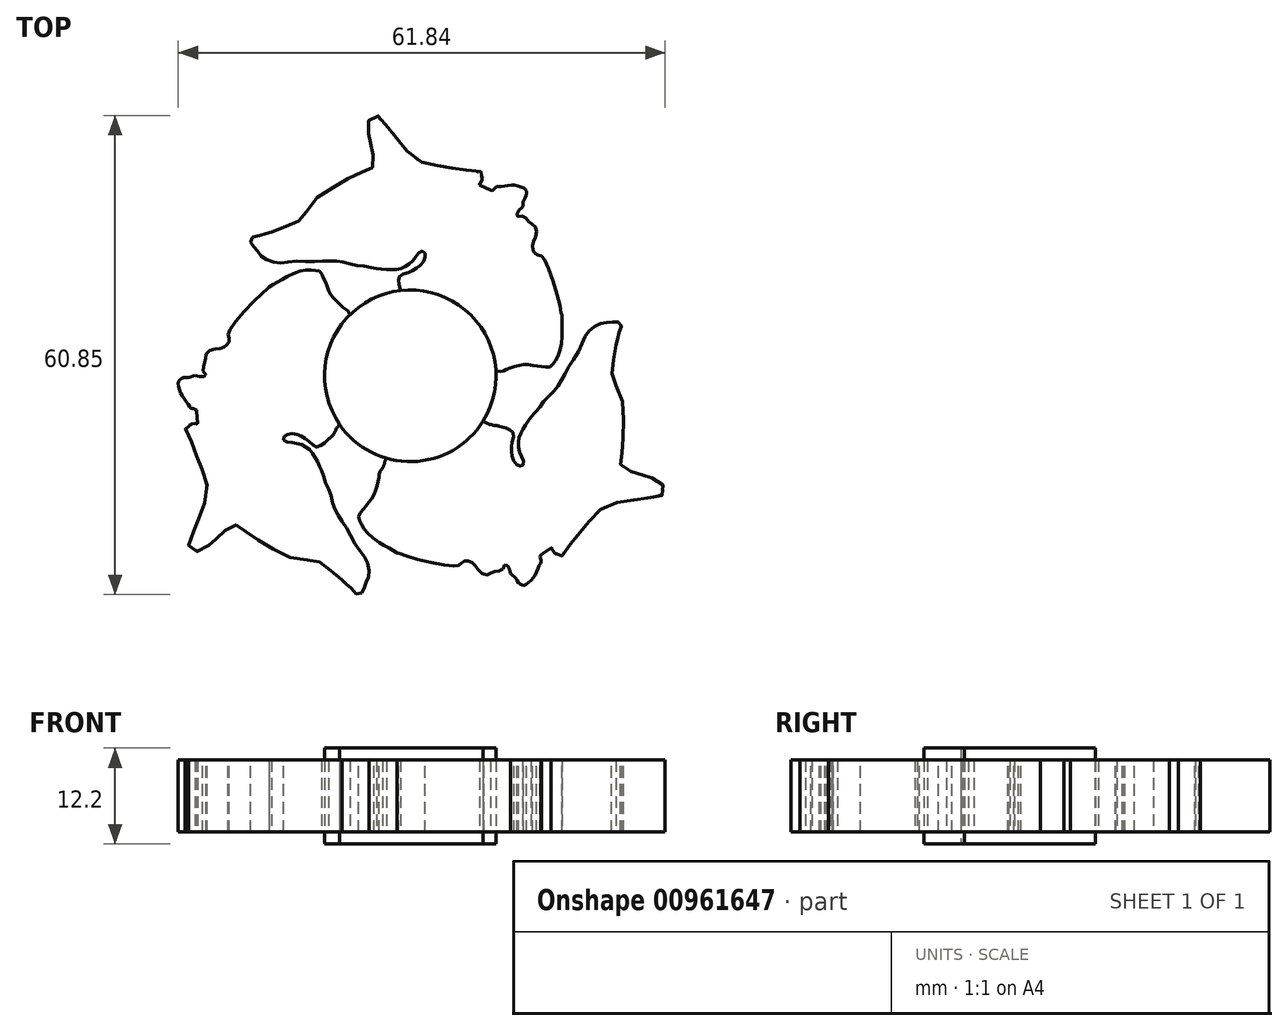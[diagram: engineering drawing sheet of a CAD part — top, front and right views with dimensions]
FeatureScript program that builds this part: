
annotation { "Feature Type Name" : "Feature", "Feature Type Description" : "" }
export const myFeature = defineFeature(function(context is Context, id is Id, definition is map)
    precondition{}
    {
        {
            var Q0;
            Q0=qCreatedBy(makeId("Top.planeOp"),FACE);
            var sketch = newSketch(context, id + "F0", { "sketchPlane" : qUnion([Q0])});
            skCircle(sketch, "E0", {"center": v(-5.45, -7.26) * mm, "radius": 10.9 * mm});
            skFitSpline(sketch, "E1", {"points": [v(-6.67, 3.57) * mm, v(-6.92, 4.58) * mm, v(-6.88, 5.09) * mm, v(-6.68, 5.56) * mm, v(-5.87, 5.8) * mm, v(-5.19, 6.1) * mm, v(-4.58, 6.45) * mm, v(-4.1, 6.82) * mm, v(-3.63, 7.5) * mm, v(-3.56, 8.14) * mm, v(-3.7, 8.48) * mm, v(-4.07, 8.55) * mm, v(-4.54, 8.14) * mm, v(-4.98, 7.53) * mm, v(-5.5, 6.99) * mm, v(-6.17, 6.58) * mm, v(-6.78, 6.3) * mm, v(-7.6, 6.24) * mm, v(-8.14, 6.2) * mm, v(-9.06, 6.3) * mm, v(-9.7, 6.34) * mm], "startDerivative": vector(-5.28, 17.85) * mm, "endDerivative": vector(-12.23, 0.24) * mm});
            skFitSpline(sketch, "E2", {"points": [v(-9.7, 6.34) * mm, v(-10.39, 6.45) * mm, v(-11.53, 6.73) * mm, v(-12.4, 6.77) * mm, v(-13.56, 7.07) * mm, v(-14.58, 7.31) * mm, v(-15.53, 7.34) * mm, v(-16.65, 7.31) * mm, v(-18, 7.24) * mm, v(-19.8, 7.31) * mm, v(-21.34, 7.16) * mm, v(-22.42, 7.1) * mm, v(-23.45, 7.39) * mm, v(-24.33, 7.89) * mm, v(-24.83, 8.5) * mm, v(-25.3, 9.11) * mm, v(-25.68, 9.65) * mm, v(-25.62, 10.26) * mm, v(-24.73, 10.54) * mm, v(-23.75, 10.84) * mm, v(-23.04, 11.01) * mm], "startDerivative": vector(-15.19, 1.76) * mm, "endDerivative": vector(16.2, 3.23) * mm});
            skFitSpline(sketch, "E3", {"points": [v(-23.04, 11.01) * mm, v(-21.41, 11.66) * mm, v(-19.99, 12.28) * mm, v(-19.13, 12.68) * mm, v(-18.16, 14.45) * mm, v(-16.28, 16.05) * mm, v(-14, 17.42) * mm, v(-12.28, 18.28) * mm, v(-10.86, 18.9) * mm, v(-10.23, 19.25) * mm, v(-10.11, 20.44) * mm, v(-10.4, 21.76) * mm, v(-10.57, 22.61) * mm, v(-10.74, 23.24) * mm, v(-10.74, 24.55) * mm, v(-10.57, 25.52) * mm, v(-9.54, 25.75) * mm, v(-8.4, 24.44) * mm, v(-7.55, 23.35) * mm, v(-6.35, 21.87) * mm, v(-4.46, 20.1) * mm, v(-2.35, 19.47) * mm, v(-0.81, 19.25) * mm, v(1, 18.96) * mm, v(2.5, 18.79) * mm, v(3.8, 18.5) * mm, v(3.8, 17.85) * mm, v(3.53, 17.52) * mm, v(3.39, 17.18) * mm, v(3.36, 16.97) * mm], "startDerivative": vector(41.16, 15.32) * mm, "endDerivative": vector(-0.65, -14.42) * mm});
            skLineSegment(sketch, "E4", {"start": v(3.36, 16.97) * mm, "end": v(4.72, 16.33) * mm});
            skFitSpline(sketch, "E5", {"points": [v(4.72, 16.33) * mm, v(4.86, 16.3) * mm, v(5.01, 16.33) * mm, v(5.18, 16.45) * mm, v(5.35, 16.64) * mm, v(5.52, 16.78) * mm, v(5.72, 16.8) * mm, v(6.45, 16.84) * mm, v(7.5, 16.96) * mm, v(8.3, 16.84) * mm, v(9.06, 16.54) * mm, v(9.26, 16.33) * mm, v(9.33, 15.94) * mm, v(9.24, 15.52) * mm, v(9, 15.08) * mm, v(8.87, 14.66) * mm, v(8.79, 14.2) * mm, v(8.78, 14.18) * mm], "startDerivative": vector(3.87, -1.54) * mm, "endDerivative": vector(-0.93, -0.4) * mm});
            skFitSpline(sketch, "E6", {"points": [v(8.79, 14.2) * mm, v(8.24, 13.6) * mm, v(8.12, 13.03) * mm, v(8.79, 13.05) * mm, v(9.4, 12.55) * mm, v(9.92, 12.07) * mm, v(10.52, 11.51) * mm, v(10.43, 10.27) * mm, v(10.09, 9.45) * mm, v(10.16, 8.73) * mm, v(10.38, 8.3) * mm, v(11, 8.03) * mm, v(11.48, 7.7) * mm, v(13.47, 2.07) * mm, v(13.8, 0.43) * mm, v(13.82, 0.43) * mm], "startDerivative": vector(-9.43, -8) * mm, "endDerivative": vector(2.22, 0.73) * mm});
            skFitSpline(sketch, "E7", {"points": [v(13.82, 0.43) * mm, v(13.82, -0.64) * mm, v(13.82, -2.3) * mm, v(13.42, -4.52) * mm, v(12.79, -5.58) * mm, v(12.22, -6.15) * mm, v(11.25, -6.06) * mm, v(10.48, -6) * mm, v(9.36, -5.83) * mm, v(8.34, -5.98) * mm, v(7.3, -6.23) * mm, v(6.54, -6.52) * mm, v(6.25, -6.7) * mm, v(5.43, -6.63) * mm], "startDerivative": vector(-0.14, -13.17) * mm, "endDerivative": vector(-14.05, 2.29) * mm});
            skFitSpline(sketch, "E8", {"points": [v(5.97, -13.68) * mm, v(6.97, -13.98) * mm, v(7.39, -14.27) * mm, v(7.7, -14.68) * mm, v(7.49, -15.5) * mm, v(7.4, -16.25) * mm, v(7.39, -16.95) * mm, v(7.47, -17.54) * mm, v(7.82, -18.3) * mm, v(8.34, -18.68) * mm, v(8.7, -18.74) * mm, v(8.95, -18.45) * mm, v(8.84, -17.83) * mm, v(8.53, -17.14) * mm, v(8.32, -16.43) * mm, v(8.31, -15.64) * mm, v(8.4, -14.97) * mm, v(8.74, -14.24) * mm, v(8.99, -13.75) * mm, v(9.54, -13.01) * mm, v(9.9, -12.48) * mm], "startDerivative": vector(18.06, -4.49) * mm, "endDerivative": vector(6.4, 10.43) * mm});
            skFitSpline(sketch, "E9", {"points": [v(9.9, -12.48) * mm, v(10.34, -11.94) * mm, v(11.15, -11.1) * mm, v(11.64, -10.36) * mm, v(12.48, -9.52) * mm, v(13.2, -8.76) * mm, v(13.71, -7.96) * mm, v(14.25, -6.97) * mm, v(14.88, -5.77) * mm, v(15.85, -4.25) * mm, v(16.5, -2.86) * mm, v(17, -1.9) * mm, v(17.76, -1.15) * mm, v(18.64, -0.65) * mm, v(19.42, -0.52) * mm, v(20.2, -0.42) * mm, v(20.85, -0.37) * mm, v(21.34, -0.74) * mm, v(21.13, -1.64) * mm, v(20.9, -2.64) * mm, v(20.68, -3.34) * mm], "startDerivative": vector(9.2, 12.2) * mm, "endDerivative": vector(-5.43, -15.6) * mm});
            skFitSpline(sketch, "E10", {"points": [v(20.68, -3.34) * mm, v(20.41, -5.07) * mm, v(20.23, -6.62) * mm, v(20.14, -7.56) * mm, v(21.17, -9.29) * mm, v(21.6, -11.72) * mm, v(21.62, -14.38) * mm, v(21.5, -16.3) * mm, v(21.31, -17.84) * mm, v(21.29, -18.56) * mm, v(22.26, -19.26) * mm, v(23.54, -19.68) * mm, v(24.37, -19.97) * mm, v(25, -20.14) * mm, v(26.12, -20.8) * mm, v(26.87, -21.44) * mm, v(26.55, -22.44) * mm, v(24.84, -22.76) * mm, v(23.47, -22.95) * mm, v(21.59, -23.23) * mm, v(19.1, -23.96) * mm, v(17.5, -25.46) * mm, v(16.52, -26.68) * mm, v(15.35, -28.09) * mm, v(14.45, -29.3) * mm, v(13.54, -30.28) * mm, v(12.99, -29.94) * mm, v(12.83, -29.55) * mm, v(12.61, -29.25) * mm, v(12.44, -29.12) * mm], "startDerivative": vector(-7.64, -43.24) * mm, "endDerivative": vector(-12.1, 7.87) * mm});
            skLineSegment(sketch, "E11", {"start": v(12.44, -29.12) * mm, "end": v(11.2, -29.97) * mm});
            skFitSpline(sketch, "E12", {"points": [v(11.2, -29.97) * mm, v(11.1, -30.07) * mm, v(11.06, -30.22) * mm, v(11.08, -30.43) * mm, v(11.15, -30.67) * mm, v(11.18, -30.88) * mm, v(11.1, -31.06) * mm, v(10.76, -31.72) * mm, v(10.34, -32.68) * mm, v(9.82, -33.32) * mm, v(9.19, -33.82) * mm, v(8.9, -33.88) * mm, v(8.54, -33.75) * mm, v(8.22, -33.46) * mm, v(7.96, -33.02) * mm, v(7.66, -32.7) * mm, v(7.3, -32.4) * mm, v(7.3, -32.38) * mm], "startDerivative": vector(-3.29, -2.55) * mm, "endDerivative": vector(0.13, 1) * mm});
            skFitSpline(sketch, "E13", {"points": [v(7.3, -32.4) * mm, v(7.07, -31.62) * mm, v(6.63, -31.23) * mm, v(6.31, -31.81) * mm, v(5.57, -32.08) * mm, v(4.9, -32.3) * mm, v(4.11, -32.53) * mm, v(3.08, -31.82) * mm, v(2.55, -31.11) * mm, v(1.9, -30.81) * mm, v(1.41, -30.78) * mm, v(0.87, -31.18) * mm, v(0.34, -31.43) * mm, v(-5.53, -30.3) * mm, v(-7.1, -29.74) * mm, v(-7.11, -29.76) * mm], "startDerivative": vector(-2.13, 12.18) * mm, "endDerivative": vector(-0.5, -2.29) * mm});
            skFitSpline(sketch, "E14", {"points": [v(-7.11, -29.76) * mm, v(-8.04, -29.22) * mm, v(-9.47, -28.38) * mm, v(-11.18, -26.9) * mm, v(-11.77, -25.83) * mm, v(-11.98, -25.05) * mm, v(-11.4, -24.25) * mm, v(-10.97, -23.62) * mm, v(-10.26, -22.74) * mm, v(-9.86, -21.79) * mm, v(-9.56, -20.77) * mm, v(-9.42, -19.96) * mm, v(-9.42, -19.63) * mm, v(-8.96, -18.95) * mm], "startDerivative": vector(-11.29, 6.8) * mm, "endDerivative": vector(9.09, 10.95) * mm});
            skLineSegment(sketch, "E15.0", {"start": v(11.2, -29.97) * mm, "end": v(8.9, -33.88) * mm, "construction": true});
            skLineSegment(sketch, "E16.0", {"start": v(-9.47, -28.38) * mm, "end": v(-7.11, -29.76) * mm, "construction": true});
            skLineSegment(sketch, "E17.0", {"start": v(6.31, -31.81) * mm, "end": v(7.3, -32.4) * mm, "construction": true});
            skFitSpline(sketch, "E18", {"points": [v(5.97, -13.68) * mm, v(5.64, -13.6) * mm, v(5.24, -13.56) * mm, v(4.98, -13.51) * mm, v(4.82, -13.46) * mm, v(4.56, -13.4) * mm, v(4.29, -13.3) * mm, v(3.81, -13) * mm, v(3.8, -13.01) * mm], "startDerivative": vector(-2.22, 0.55) * mm, "endDerivative": vector(-0.03, -0.43) * mm});
            skFitSpline(sketch, "E19", {"points": [v(-8.96, -18.95) * mm, v(-8.82, -18.65) * mm, v(-8.72, -18.4) * mm, v(-8.69, -18.2) * mm, v(-8.61, -17.97) * mm, v(-8.54, -17.83) * mm, v(-8.48, -17.73) * mm], "startDerivative": vector(0.65, 1.48) * mm, "endDerivative": vector(0.53, 0.83) * mm});
            skFitSpline(sketch, "E20", {"points": [v(-15.83, -15.28) * mm, v(-16.58, -16) * mm, v(-17.04, -16.22) * mm, v(-17.55, -16.28) * mm, v(-18.16, -15.7) * mm, v(-18.77, -15.26) * mm, v(-19.37, -14.9) * mm, v(-19.93, -14.68) * mm, v(-20.75, -14.6) * mm, v(-21.34, -14.87) * mm, v(-21.57, -15.16) * mm, v(-21.44, -15.51) * mm, v(-20.85, -15.72) * mm, v(-20.1, -15.8) * mm, v(-19.38, -15.97) * mm, v(-18.69, -16.35) * mm, v(-18.14, -16.74) * mm, v(-17.68, -17.42) * mm, v(-17.38, -17.87) * mm, v(-17, -18.71) * mm, v(-16.72, -19.29) * mm], "startDerivative": vector(-12.82, -13.5) * mm, "endDerivative": vector(5.9, -10.71) * mm});
            skFitSpline(sketch, "E21", {"points": [v(-16.72, -19.29) * mm, v(-16.47, -19.94) * mm, v(-16.13, -21.06) * mm, v(-15.73, -21.85) * mm, v(-15.42, -23) * mm, v(-15.11, -24) * mm, v(-14.67, -24.84) * mm, v(-14.08, -25.8) * mm, v(-13.34, -26.93) * mm, v(-12.5, -28.52) * mm, v(-11.6, -29.77) * mm, v(-11.01, -30.68) * mm, v(-10.74, -31.71) * mm, v(-10.74, -32.73) * mm, v(-11.02, -33.47) * mm, v(-11.3, -34.2) * mm, v(-11.6, -34.78) * mm, v(-12.15, -35.03) * mm, v(-12.83, -34.4) * mm, v(-13.59, -33.7) * mm, v(-14.1, -33.17) * mm], "startDerivative": vector(6.07, -14.03) * mm, "endDerivative": vector(-10.9, 12.42) * mm});
            skFitSpline(sketch, "E22", {"points": [v(-14.1, -33.17) * mm, v(-15.46, -32.09) * mm, v(-16.72, -31.17) * mm, v(-17.5, -30.62) * mm, v(-19.5, -30.67) * mm, v(-21.83, -29.84) * mm, v(-24.16, -28.55) * mm, v(-25.76, -27.5) * mm, v(-27.01, -26.57) * mm, v(-27.63, -26.2) * mm, v(-28.72, -26.7) * mm, v(-29.71, -27.6) * mm, v(-30.37, -28.18) * mm, v(-30.83, -28.64) * mm, v(-31.96, -29.3) * mm, v(-32.9, -29.63) * mm, v(-33.6, -28.86) * mm, v(-33.04, -27.21) * mm, v(-32.52, -25.93) * mm, v(-31.84, -24.15) * mm, v(-31.25, -21.63) * mm, v(-31.76, -19.5) * mm, v(-32.33, -18.04) * mm, v(-32.99, -16.33) * mm, v(-33.6, -14.95) * mm, v(-34, -13.67) * mm, v(-33.43, -13.36) * mm, v(-33, -13.42) * mm, v(-32.65, -13.37) * mm, v(-32.45, -13.29) * mm], "startDerivative": vector(-33.84, 27.98) * mm, "endDerivative": vector(12.81, 6.65) * mm});
            skLineSegment(sketch, "E23", {"start": v(-32.45, -13.29) * mm, "end": v(-32.57, -11.8) * mm});
            skFitSpline(sketch, "E24", {"points": [v(-32.57, -11.8) * mm, v(-32.61, -11.65) * mm, v(-32.72, -11.54) * mm, v(-32.91, -11.46) * mm, v(-33.16, -11.4) * mm, v(-33.36, -11.32) * mm, v(-33.47, -11.16) * mm, v(-33.88, -10.55) * mm, v(-34.5, -9.7) * mm, v(-34.8, -8.94) * mm, v(-34.93, -8.14) * mm, v(-34.84, -7.87) * mm, v(-34.54, -7.6) * mm, v(-34.14, -7.47) * mm, v(-33.63, -7.47) * mm, v(-33.2, -7.36) * mm, v(-32.76, -7.2) * mm, v(-32.74, -7.2) * mm], "startDerivative": vector(-0.6, 4.12) * mm, "endDerivative": vector(0.8, -0.6) * mm});
            skFitSpline(sketch, "E25", {"points": [v(-32.76, -7.2) * mm, v(-31.97, -7.38) * mm, v(-31.41, -7.2) * mm, v(-31.77, -6.63) * mm, v(-31.63, -5.85) * mm, v(-31.48, -5.16) * mm, v(-31.3, -4.36) * mm, v(-30.18, -3.82) * mm, v(-29.3, -3.7) * mm, v(-28.71, -3.28) * mm, v(-28.45, -2.88) * mm, v(-28.53, -2.2) * mm, v(-28.48, -1.62) * mm, v(-24.6, 2.92) * mm, v(-23.35, 4.02) * mm, v(-23.36, 4.03) * mm], "startDerivative": vector(11.65, -4.16) * mm, "endDerivative": vector(-1.75, 1.56) * mm});
            skFitSpline(sketch, "E26", {"points": [v(-23.36, 4.03) * mm, v(-22.43, 4.57) * mm, v(-21, 5.4) * mm, v(-18.86, 6.16) * mm, v(-17.64, 6.15) * mm, v(-16.86, 5.94) * mm, v(-16.45, 5.06) * mm, v(-16.1, 4.36) * mm, v(-15.7, 3.31) * mm, v(-15.06, 2.5) * mm, v(-14.33, 1.73) * mm, v(-13.7, 1.2) * mm, v(-13.4, 1.04) * mm, v(-13.04, 0.3) * mm], "startDerivative": vector(11.48, 6.47) * mm, "endDerivative": vector(5.04, -13.3) * mm});
            skLineSegment(sketch, "E27.0", {"start": v(-32.57, -11.8) * mm, "end": v(-34.84, -7.87) * mm, "construction": true});
            skLineSegment(sketch, "E28.0", {"start": v(-21, 5.4) * mm, "end": v(-23.36, 4.03) * mm, "construction": true});
            skLineSegment(sketch, "E29.0", {"start": v(-31.77, -6.63) * mm, "end": v(-32.76, -7.2) * mm, "construction": true});
            skFitSpline(sketch, "E30", {"points": [v(-15.83, -15.28) * mm, v(-15.38, -14.93) * mm, v(-15.03, -14.42) * mm, v(-14.78, -13.87) * mm, v(-14.43, -13.44) * mm, v(-14.43, -13.43) * mm], "startDerivative": vector(1.93, 1.34) * mm, "endDerivative": vector(-0.32, 0.2) * mm});
            skSolve(sketch);
        }
        {
            var Q0;
            {var subQ0=sQuery(id+"F0.wireOp",EDGE,"E1");Q0=makeQuery(id+"F0.imprint","IMPRINT",FACE,{"disambiguationData":[TD([[makeQuery(id+"F0.imprint","IMPRINT",EDGE,{"derivedFrom":subQ0}),-1.0]])]});}
            var Q1;
            {var subQ0=sQuery(id+"F0.wireOp",EDGE,"E20");Q1=makeQuery(id+"F0.imprint","IMPRINT",FACE,{"disambiguationData":[TD([[makeQuery(id+"F0.imprint","IMPRINT",EDGE,{"derivedFrom":subQ0}),-1.0]])]});}
            var Q2;
            {var subQ1=sQuery(id+"F0.wireOp",EDGE,"E8");Q2=makeQuery(id+"F0.imprint","IMPRINT",FACE,{"disambiguationData":[TD([[makeQuery(id+"F0.imprint","IMPRINT",EDGE,{"derivedFrom":subQ1}),-1.0]])]});}
            extrude(context, id + "F1", {"entities" : qUnion([Q0, Q1, Q2]), "endBound" : BoundingType.SYMMETRIC, "depth" : 9.14 * mm, "offsetDistance" : 25.4 * mm});
        }
        {
            var Q0;
            {var subQ0=sQuery(id+"F0.wireOp",EDGE,"E0");var subQ6=makeQuery(id+"F0.imprint","INTERSECT",VERTEX,{"derivedFrom":[subQ0,sQuery(id+"F0.wireOp",EDGE,"E1")]});Q0=makeQuery(id+"F0.imprint","IMPRINT",FACE,{"disambiguationData":[TD([[makeQuery(id+"F0.imprint","IMPRINT",EDGE,{"disambiguationData":[TD([[subQ6,1.0]])],"derivedFrom":subQ0}),1.0]])]});}
            extrude(context, id + "F2", {"entities" : qUnion([Q0]), "endBound" : BoundingType.SYMMETRIC, "depth" : 12.2 * mm, "offsetDistance" : 25.4 * mm});
        }
    });
